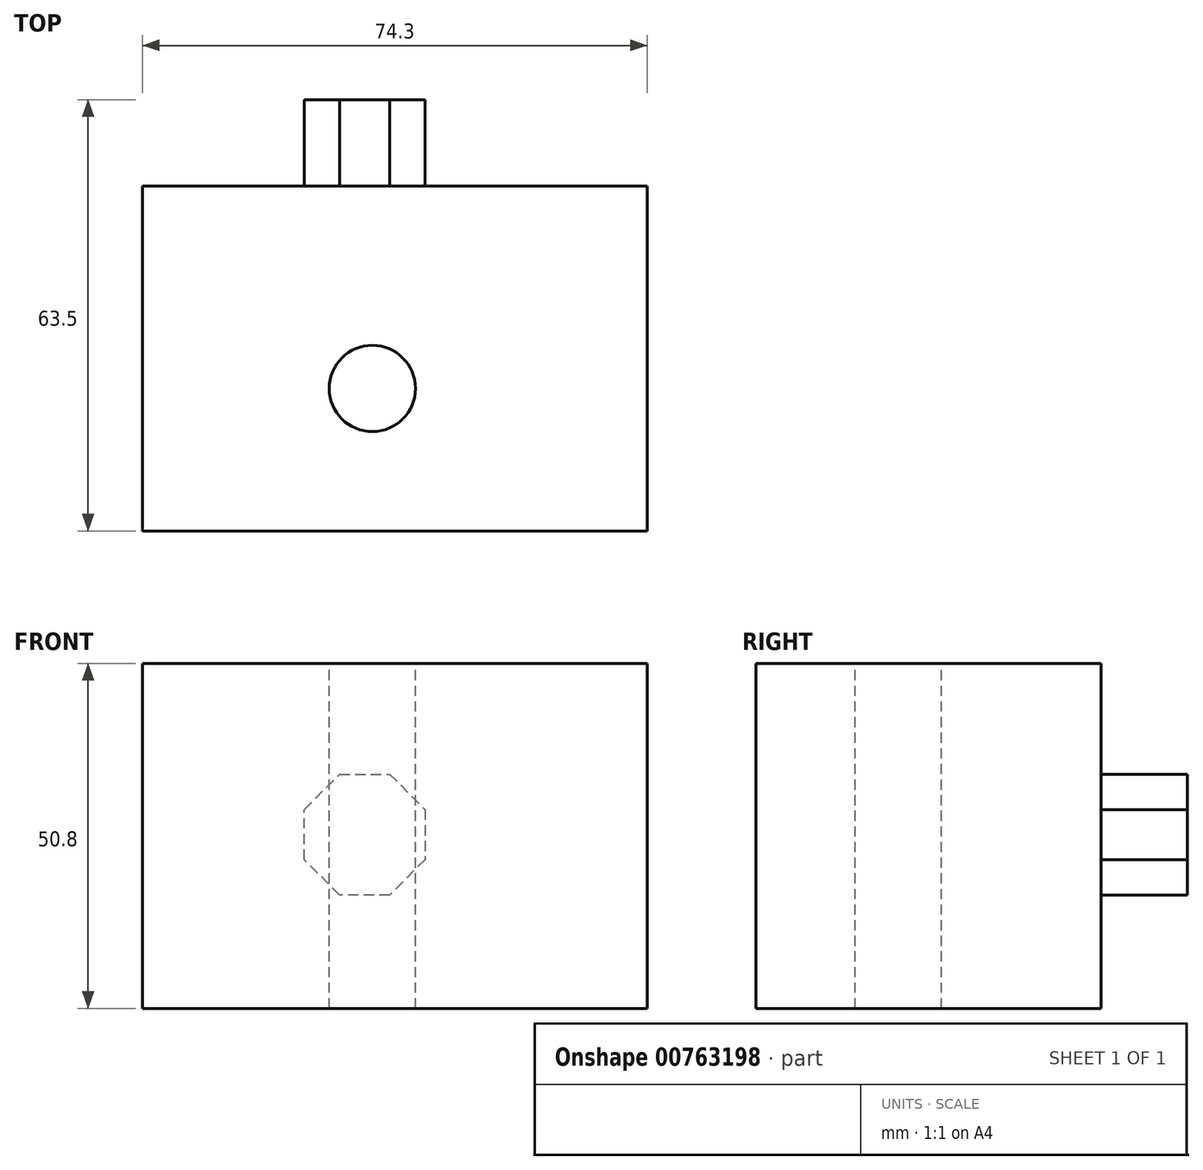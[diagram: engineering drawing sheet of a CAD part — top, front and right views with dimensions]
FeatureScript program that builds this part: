
annotation { "Feature Type Name" : "Feature", "Feature Type Description" : "" }
export const myFeature = defineFeature(function(context is Context, id is Id, definition is map)
    precondition{}
    {
        {
            var Q0;
            Q0=qCreatedBy(makeId("Front.planeOp"),FACE);
            var sketch = newSketch(context, id + "F0", { "sketchPlane" : qUnion([Q0])});
            skLineSegment(sketch, "E0.bottom", {"start": v(-82, 53.56) * mm, "end": v(-7.69, 53.56) * mm});
            skLineSegment(sketch, "E0.top", {"start": v(-82, 2.76) * mm, "end": v(-7.69, 2.76) * mm});
            skLineSegment(sketch, "E0.left", {"start": v(-82, 53.56) * mm, "end": v(-82, 2.76) * mm});
            skLineSegment(sketch, "E0.right", {"start": v(-7.69, 53.56) * mm, "end": v(-7.69, 2.76) * mm});
            skSolve(sketch);
        }
        {
            var Q0;
            Q0=makeQuery(id+"F0.imprint","IMPRINT",FACE,{"disambiguationData":[TD([[makeQuery(id+"F0.imprint","IMPRINT",EDGE,{"derivedFrom":sQuery(id+"F0.wireOp",EDGE,"E0.bottom")}),-1.0]])]});
            extrude(context, id + "F1", {"entities" : qUnion([Q0]), "depth" : 50.8 * mm, "offsetDistance" : 25.4 * mm});
        }
        {
            var Q0;
            Q0=makeQuery(id+"F1.opExtrude","SWEPT_FACE",FACE,{"disambiguationData":[OSD([sQuery(id+"F0.wireOp",EDGE,"E0.left")])]});
            var sketch = newSketch(context, id + "F2", { "sketchPlane" : qUnion([Q0])});
            skFitSpline(sketch, "E1", {"points": [v(14.88, 44.82) * mm, v(36.41, 34.18) * mm, v(15.97, 17.62) * mm, v(38.93, 9.9) * mm, v(35.63, 20.3) * mm, v(45.24, 36.06) * mm, v(27.98, 50.28) * mm, v(4.5, 43.11) * mm, v(16.87, 30.2) * mm, v(20.61, 34.21) * mm, v(9.86, 42.47) * mm, v(14.88, 44.82) * mm]});
            skSolve(sketch);
        }
        {
            var Q0;
            Q0=sQuery(id+"F2.wireOp",EDGE,"E1");
            extrude(context, id + "F3", {"bodyType" : ToolBodyType.SURFACE, "surfaceEntities" : qUnion([Q0]), "depth" : 12.7 * mm, "offsetDistance" : 25.4 * mm});
        }
        {
            var Q0;
            Q0=makeQuery(id+"F1.opExtrude","SWEPT_FACE",FACE,{"disambiguationData":[OSD([sQuery(id+"F0.wireOp",EDGE,"E0.bottom")])]});
            var sketch = newSketch(context, id + "F4", { "sketchPlane" : qUnion([Q0])});
            skPoint(sketch, "E2", {"position": v(-48.16, -29.84) * mm});
            skSolve(sketch);
        }
        {
            var Q0;
            Q0=sQuery(id+"F4.wireOp",VERTEX,"E2");
            var Q1;
            Q1=makeQuery(id+"F1.opExtrude","SWEPT_BODY",BODY,{"disambiguationData":[OSD([sQuery(id+"F0.wireOp",EDGE,"E0.bottom"),sQuery(id+"F0.wireOp",EDGE,"E0.top"),sQuery(id+"F0.wireOp",EDGE,"E0.left"),sQuery(id+"F0.wireOp",EDGE,"E0.right")])]});
            hole(context, id + "F5", {"style" : HoleStyle.SIMPLE, "endStyle" : HoleEndStyle.THROUGH, "holeDiameter" : 12.7 * mm, "majorDiameter" : 6.35 * mm, "isTappedThrough" : true, "tappedDepth" : 12.7 * mm, "tapClearance" : 3, "locations" : qUnion([Q0]), "scope" : qUnion([Q1])});
        }
        {
            var Q0;
            Q0=makeQuery(id+"F0.imprint","IMPRINT",FACE,{"disambiguationData":[TD([[makeQuery(id+"F0.imprint","IMPRINT",EDGE,{"derivedFrom":sQuery(id+"F0.wireOp",EDGE,"E0.bottom")}),-1.0]])]});
            var sketch = newSketch(context, id + "F6", { "sketchPlane" : qUnion([Q0])});
            skCircle(sketch, "E3.cCircle", {"center": v(-49.3, 28.34) * mm, "radius": 8.9 * mm, "construction": true});
            skLineSegment(sketch, "E3.0", {"start": v(-45.6, 37.23) * mm, "end": v(-40.4, 32.02) * mm});
            skLineSegment(sketch, "E3.1", {"start": v(-40.4, 32.02) * mm, "end": v(-40.4, 24.65) * mm});
            skLineSegment(sketch, "E3.2", {"start": v(-40.4, 24.65) * mm, "end": v(-45.61, 19.45) * mm});
            skLineSegment(sketch, "E3.3", {"start": v(-45.61, 19.45) * mm, "end": v(-52.98, 19.45) * mm});
            skLineSegment(sketch, "E3.4", {"start": v(-52.98, 19.45) * mm, "end": v(-58.18, 24.66) * mm});
            skLineSegment(sketch, "E3.5", {"start": v(-58.18, 24.66) * mm, "end": v(-58.18, 32.02) * mm});
            skLineSegment(sketch, "E3.6", {"start": v(-58.18, 32.02) * mm, "end": v(-52.97, 37.23) * mm});
            skLineSegment(sketch, "E3.7", {"start": v(-52.97, 37.23) * mm, "end": v(-45.6, 37.23) * mm});
            skPoint(sketch, "E3.0.midPoint", {"position": v(-43, 34.63) * mm});
            skSolve(sketch);
        }
        {
            var Q0;
            Q0=makeQuery(id+"F6.imprint","IMPRINT",FACE,{"disambiguationData":[TD([[makeQuery(id+"F6.imprint","IMPRINT",EDGE,{"derivedFrom":sQuery(id+"F6.wireOp",EDGE,"E3.0")}),-1.0]])]});
            extrude(context, id + "F7", {"entities" : qUnion([Q0]), "oppositeDirection" : true, "depth" : 12.7 * mm, "offsetDistance" : 25.4 * mm});
        }
    });
